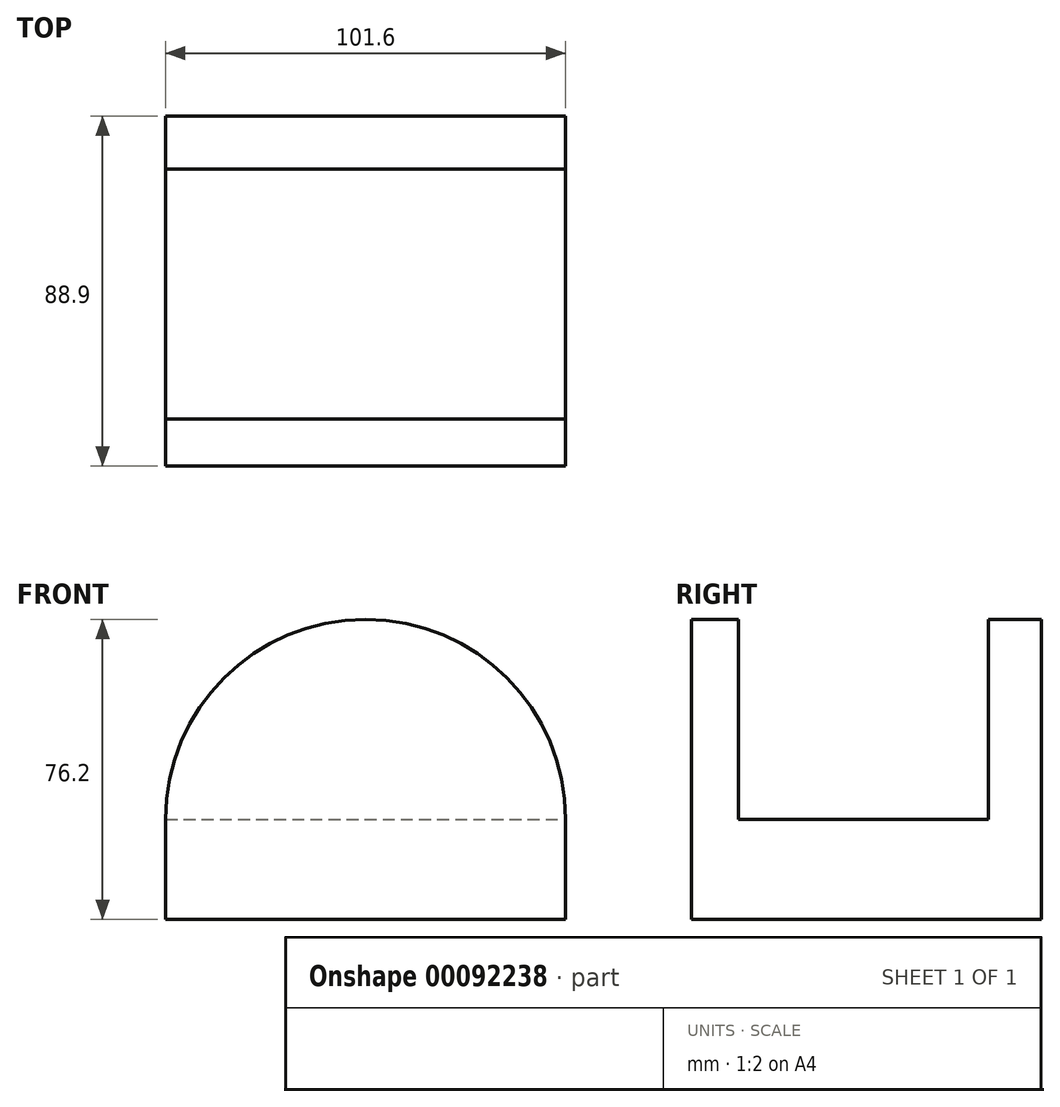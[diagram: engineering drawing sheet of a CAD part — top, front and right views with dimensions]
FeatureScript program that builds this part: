
annotation { "Feature Type Name" : "Feature", "Feature Type Description" : "" }
export const myFeature = defineFeature(function(context is Context, id is Id, definition is map)
    precondition{}
    {
        {
            var Q0;
            Q0=qCreatedBy(makeId("Front.planeOp"),FACE);
            var sketch = newSketch(context, id + "F0", { "sketchPlane" : qUnion([Q0])});
            skLineSegment(sketch, "E0.top", {"start": v(-50.8, -12.7) * mm, "end": v(50.8, -12.7) * mm});
            skLineSegment(sketch, "E0.left", {"start": v(-50.8, 12.7) * mm, "end": v(-50.8, -12.7) * mm});
            skLineSegment(sketch, "E0.right", {"start": v(50.8, 12.7) * mm, "end": v(50.8, -12.7) * mm});
            skArc(sketch, "E1", {"start": v(50.8, 12.7) * mm, "mid": v(0, 63.5) * mm, "end": v(-50.8, 12.7) * mm});
            skSolve(sketch);
        }
        {
            var Q0;
            Q0 = qSketchRegion(id + "F0", true);
            extrude(context, id + "F1", {"entities" : qUnion([Q0]), "endBound" : BoundingType.SYMMETRIC, "depth" : 88.9 * mm});
        }
        {
            var Q0;
            Q0=qCreatedBy(makeId("Right.planeOp"),FACE);
            var sketch = newSketch(context, id + "F2", { "sketchPlane" : qUnion([Q0])});
            skLineSegment(sketch, "E2.bottom", {"start": v(30.95, 63.5) * mm, "end": v(-32.55, 63.5) * mm});
            skLineSegment(sketch, "E2.top", {"start": v(30.95, 12.7) * mm, "end": v(-32.55, 12.7) * mm});
            skLineSegment(sketch, "E2.left", {"start": v(30.95, 63.5) * mm, "end": v(30.95, 12.7) * mm});
            skLineSegment(sketch, "E2.right", {"start": v(-32.55, 63.5) * mm, "end": v(-32.55, 12.7) * mm});
            skSolve(sketch);
        }
        {
            var Q0;
            Q0 = qSketchRegion(id + "F2", true);
            extrude(context, id + "F3", {"entities" : qUnion([Q0]), "operationType" : NewBodyOperationType.REMOVE, "endBound" : BoundingType.SYMMETRIC, "oppositeDirection" : true, "depth" : 101.6 * mm});
        }
    });
